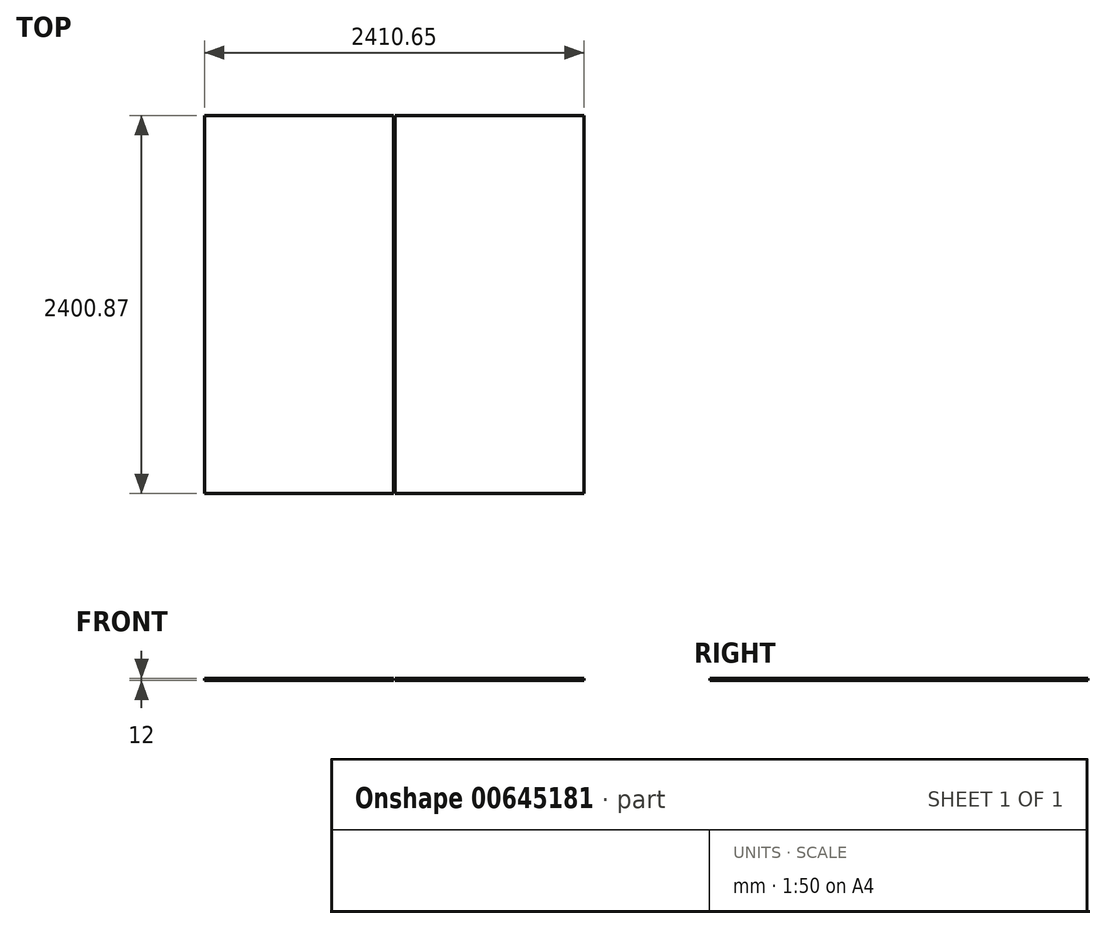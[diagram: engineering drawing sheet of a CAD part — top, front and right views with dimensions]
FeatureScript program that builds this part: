
annotation { "Feature Type Name" : "Feature", "Feature Type Description" : "" }
export const myFeature = defineFeature(function(context is Context, id is Id, definition is map)
    precondition{}
    {
        {
            var Q0;
            Q0=qCreatedBy(makeId("Top.planeOp"),FACE);
            var sketch = newSketch(context, id + "F0", { "sketchPlane" : qUnion([Q0])});
            skLineSegment(sketch, "E0.bottom", {"start": v(4.11, 2401.67) * mm, "end": v(1204.11, 2401.67) * mm});
            skLineSegment(sketch, "E0.top", {"start": v(4.11, 1.67) * mm, "end": v(1204.11, 1.67) * mm});
            skLineSegment(sketch, "E0.left", {"start": v(4.11, 2401.67) * mm, "end": v(4.11, 1.67) * mm});
            skLineSegment(sketch, "E0.right", {"start": v(1204.11, 2401.67) * mm, "end": v(1204.11, 1.67) * mm});
            skSolve(sketch);
        }
        {
            var Q0;
            Q0=makeQuery(id+"F0.imprint","IMPRINT",FACE,{"disambiguationData":[TD([[makeQuery(id+"F0.imprint","IMPRINT",EDGE,{"derivedFrom":sQuery(id+"F0.wireOp",EDGE,"E0.bottom")}),-1.0]])]});
            extrude(context, id + "F1", {"entities" : qUnion([Q0]), "depth" : 12 * mm, "offsetDistance" : 25 * mm});
        }
        {
            var Q0;
            Q0=qCreatedBy(makeId("Top.planeOp"),FACE);
            var sketch = newSketch(context, id + "F2", { "sketchPlane" : qUnion([Q0])});
            skLineSegment(sketch, "E1.bottom", {"start": v(-1206.54, 2400.8) * mm, "end": v(-6.54, 2400.8) * mm});
            skLineSegment(sketch, "E1.top", {"start": v(-1206.54, 0.8) * mm, "end": v(-6.54, 0.8) * mm});
            skLineSegment(sketch, "E1.left", {"start": v(-1206.54, 2400.8) * mm, "end": v(-1206.54, 0.8) * mm});
            skLineSegment(sketch, "E1.right", {"start": v(-6.54, 2400.8) * mm, "end": v(-6.54, 0.8) * mm});
            skSolve(sketch);
        }
        {
            var Q0;
            Q0 = qSketchRegion(id + "F2", true);
            extrude(context, id + "F3", {"entities" : qUnion([Q0]), "depth" : 12 * mm, "offsetDistance" : 25 * mm});
        }
    });
